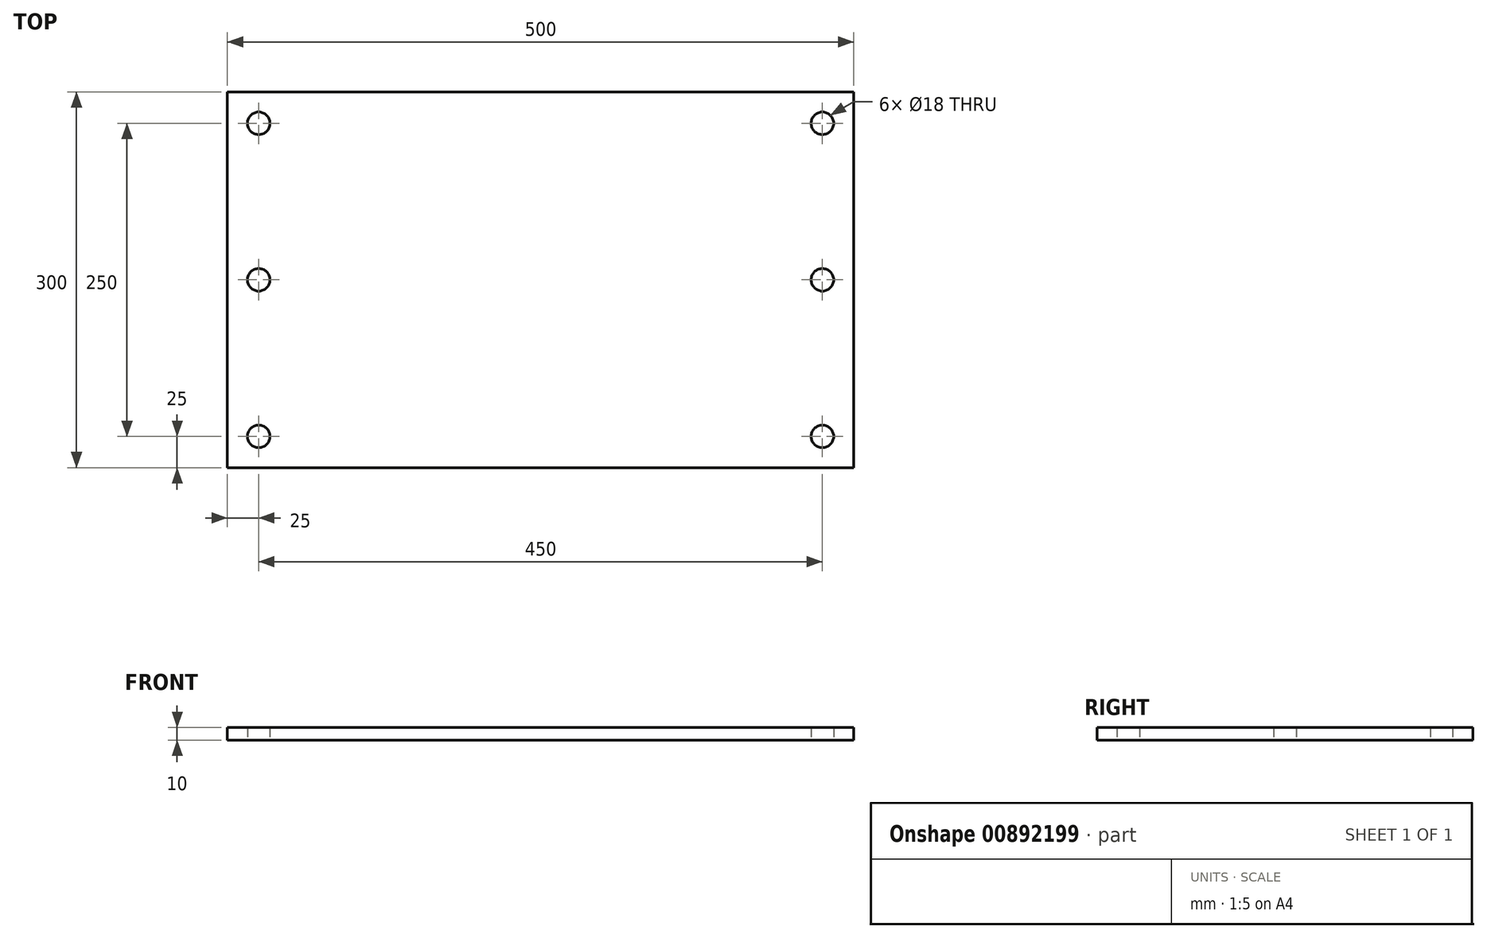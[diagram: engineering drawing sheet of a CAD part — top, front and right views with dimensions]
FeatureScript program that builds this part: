
annotation { "Feature Type Name" : "Feature", "Feature Type Description" : "" }
export const myFeature = defineFeature(function(context is Context, id is Id, definition is map)
    precondition{}
    {
        {
            var Q0;
            Q0=qCreatedBy(makeId("Top.planeOp"),FACE);
            var sketch = newSketch(context, id + "F0", { "sketchPlane" : qUnion([Q0])});
            skLineSegment(sketch, "E0.bottom", {"start": v(0, 0) * mm, "end": v(500, 0) * mm});
            skLineSegment(sketch, "E0.top", {"start": v(0, 300) * mm, "end": v(500, 300) * mm});
            skLineSegment(sketch, "E0.left", {"start": v(0, 0) * mm, "end": v(0, 300) * mm});
            skLineSegment(sketch, "E0.right", {"start": v(500, 0) * mm, "end": v(500, 300) * mm});
            skCircle(sketch, "E1", {"center": v(475, 275) * mm, "radius": 9 * mm});
            skCircle(sketch, "E2", {"center": v(25, 275) * mm, "radius": 9 * mm});
            skCircle(sketch, "E3.0.1.0", {"center": v(475, 150) * mm, "radius": 9 * mm});
            skCircle(sketch, "E3.0.1.1", {"center": v(25, 150) * mm, "radius": 9 * mm});
            skCircle(sketch, "E3.0.2.0", {"center": v(475, 25) * mm, "radius": 9 * mm});
            skCircle(sketch, "E3.0.2.1", {"center": v(25, 25) * mm, "radius": 9 * mm});
            skLineSegment(sketch, "E3.direction1", {"start": v(475, 275) * mm, "end": v(500, 275) * mm, "construction": true});
            skLineSegment(sketch, "E3.direction2", {"start": v(475, 275) * mm, "end": v(475, 150) * mm, "construction": true});
            skSolve(sketch);
        }
        {
            var Q0;
            Q0=makeQuery(id+"F0.imprint","IMPRINT",FACE,{"disambiguationData":[TD([[makeQuery(id+"F0.imprint","IMPRINT",EDGE,{"derivedFrom":sQuery(id+"F0.wireOp",EDGE,"E0.bottom")}),1.0]])]});
            extrude(context, id + "F1", {"entities" : qUnion([Q0]), "depth" : 10 * mm, "offsetDistance" : 25 * mm});
        }
    });
